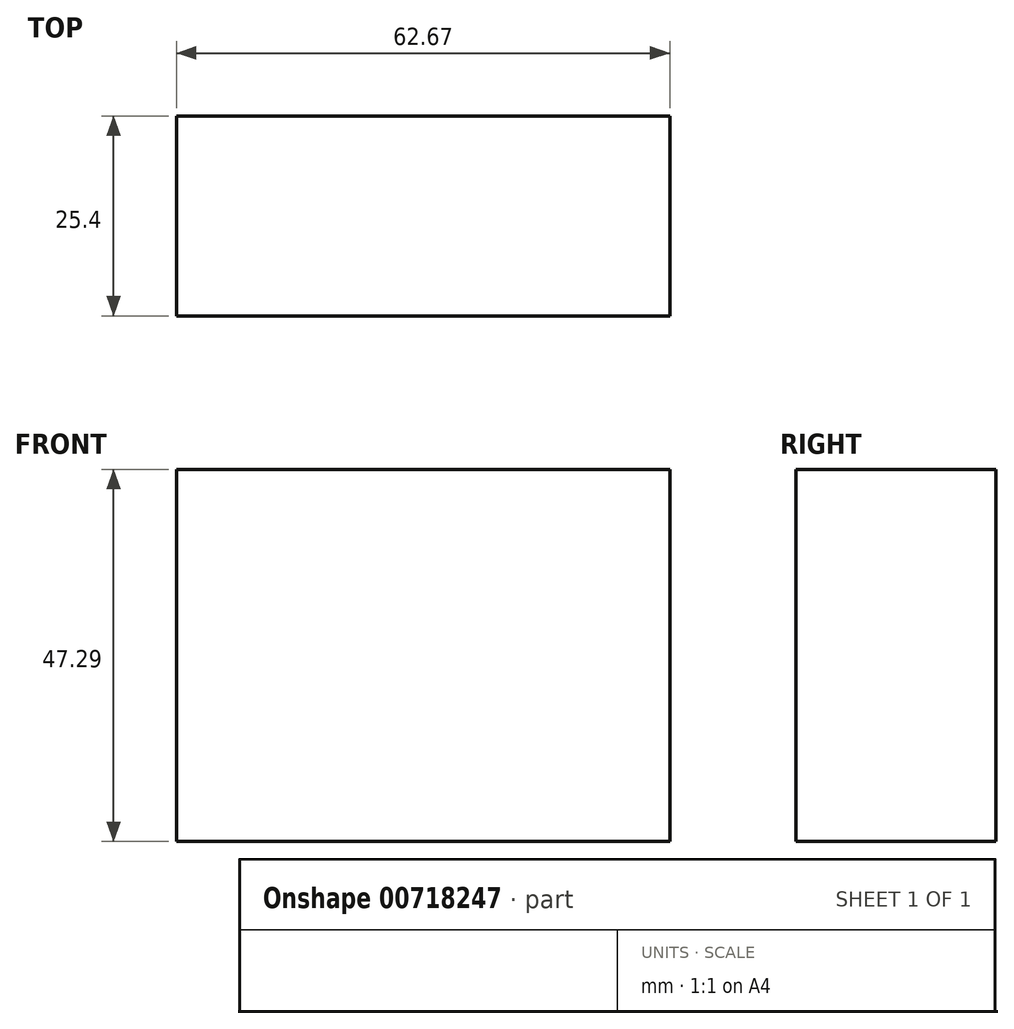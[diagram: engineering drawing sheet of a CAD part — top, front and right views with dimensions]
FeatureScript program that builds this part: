
annotation { "Feature Type Name" : "Feature", "Feature Type Description" : "" }
export const myFeature = defineFeature(function(context is Context, id is Id, definition is map)
    precondition{}
    {
        {
            var Q0;
            Q0=qCreatedBy(makeId("Front.planeOp"),FACE);
            var sketch = newSketch(context, id + "F0", { "sketchPlane" : qUnion([Q0])});
            skLineSegment(sketch, "E0.bottom", {"start": v(0, 0) * mm, "end": v(62.67, 0) * mm});
            skLineSegment(sketch, "E0.top", {"start": v(0, 47.3) * mm, "end": v(62.67, 47.3) * mm});
            skLineSegment(sketch, "E0.left", {"start": v(0, 0) * mm, "end": v(0, 47.3) * mm});
            skLineSegment(sketch, "E0.right", {"start": v(62.67, 0) * mm, "end": v(62.67, 47.3) * mm});
            skSolve(sketch);
        }
        {
            var Q0;
            Q0 = qSketchRegion(id + "F0", true);
            extrude(context, id + "F1", {"entities" : qUnion([Q0]), "depth" : 25.4 * mm, "offsetDistance" : 25.4 * mm});
        }
    });
